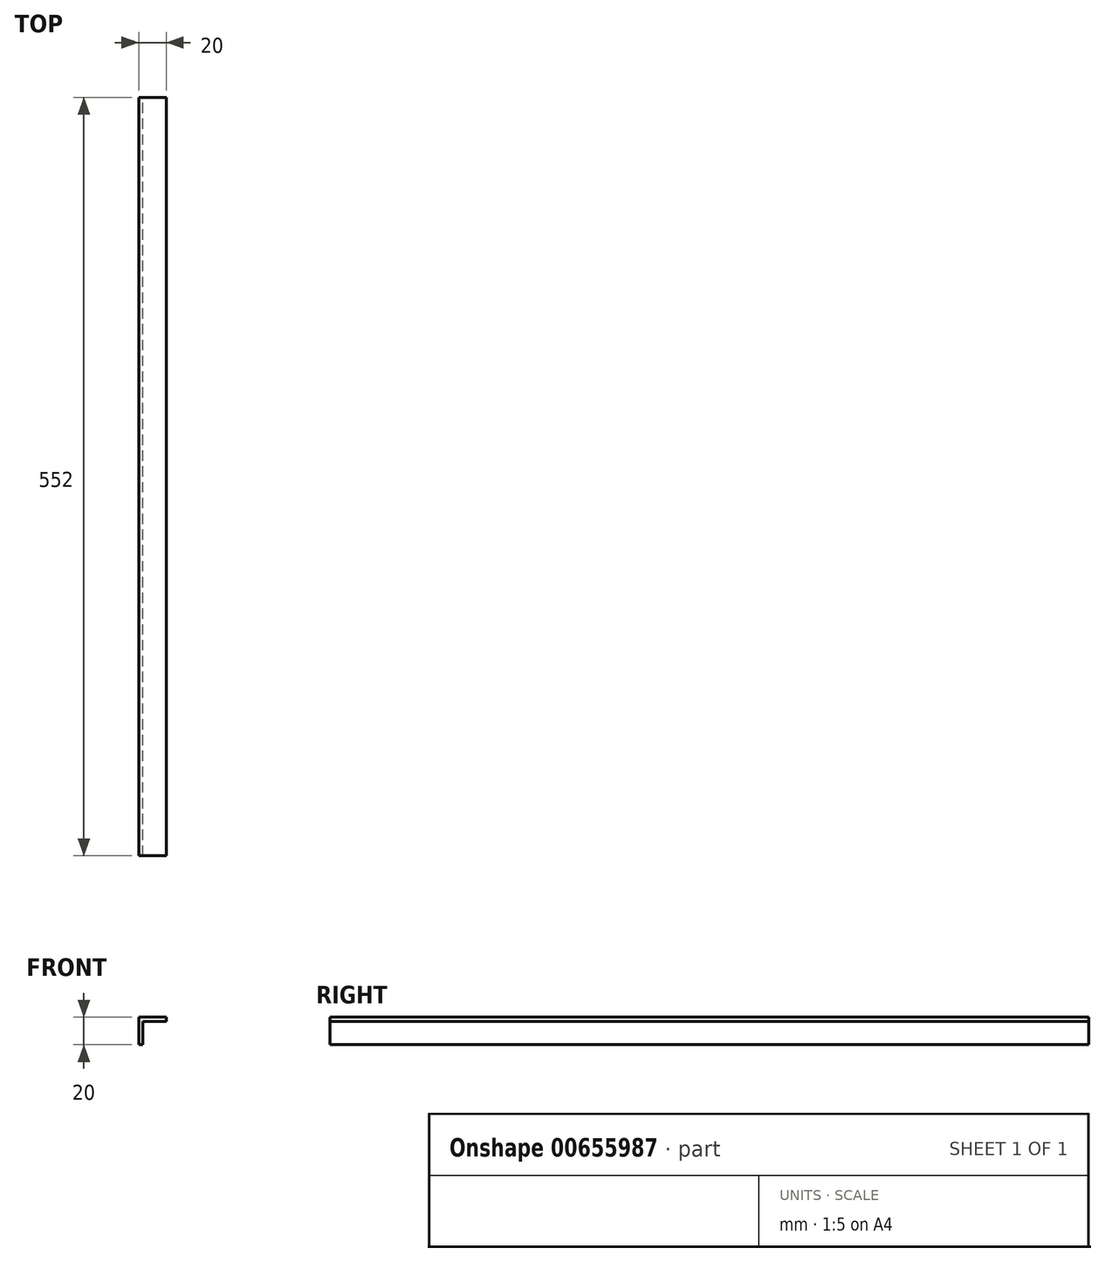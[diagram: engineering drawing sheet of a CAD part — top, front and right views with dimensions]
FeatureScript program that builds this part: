
annotation { "Feature Type Name" : "Feature", "Feature Type Description" : "" }
export const myFeature = defineFeature(function(context is Context, id is Id, definition is map)
    precondition{}
    {
        {
            var Q0;
            Q0=qCreatedBy(makeId("Front.planeOp"),FACE);
            var sketch = newSketch(context, id + "F0", { "sketchPlane" : qUnion([Q0])});
            skLineSegment(sketch, "E0", {"start": v(0, 0) * mm, "end": v(0, 20) * mm});
            skLineSegment(sketch, "E1", {"start": v(0, 20) * mm, "end": v(20, 20) * mm});
            skLineSegment(sketch, "E2.0", {"start": v(3, 17) * mm, "end": v(20, 17) * mm});
            skLineSegment(sketch, "E2.1", {"start": v(3, 0) * mm, "end": v(3, 17) * mm});
            skLineSegment(sketch, "E3", {"start": v(20, 20) * mm, "end": v(20, 17) * mm});
            skLineSegment(sketch, "E4", {"start": v(0, 0) * mm, "end": v(3, 0) * mm});
            skSolve(sketch);
        }
        {
            var Q0;
            Q0=makeQuery(id+"F0.imprint","IMPRINT",FACE,{"disambiguationData":[TD([[makeQuery(id+"F0.imprint","IMPRINT",EDGE,{"derivedFrom":sQuery(id+"F0.wireOp",EDGE,"E0")}),-1.0]])]});
            extrude(context, id + "F1", {"entities" : qUnion([Q0]), "depth" : 600 * mm - 4 * mm - 4 * mm - 40 * mm, "offsetDistance" : 25.4 * mm});
        }
    });
